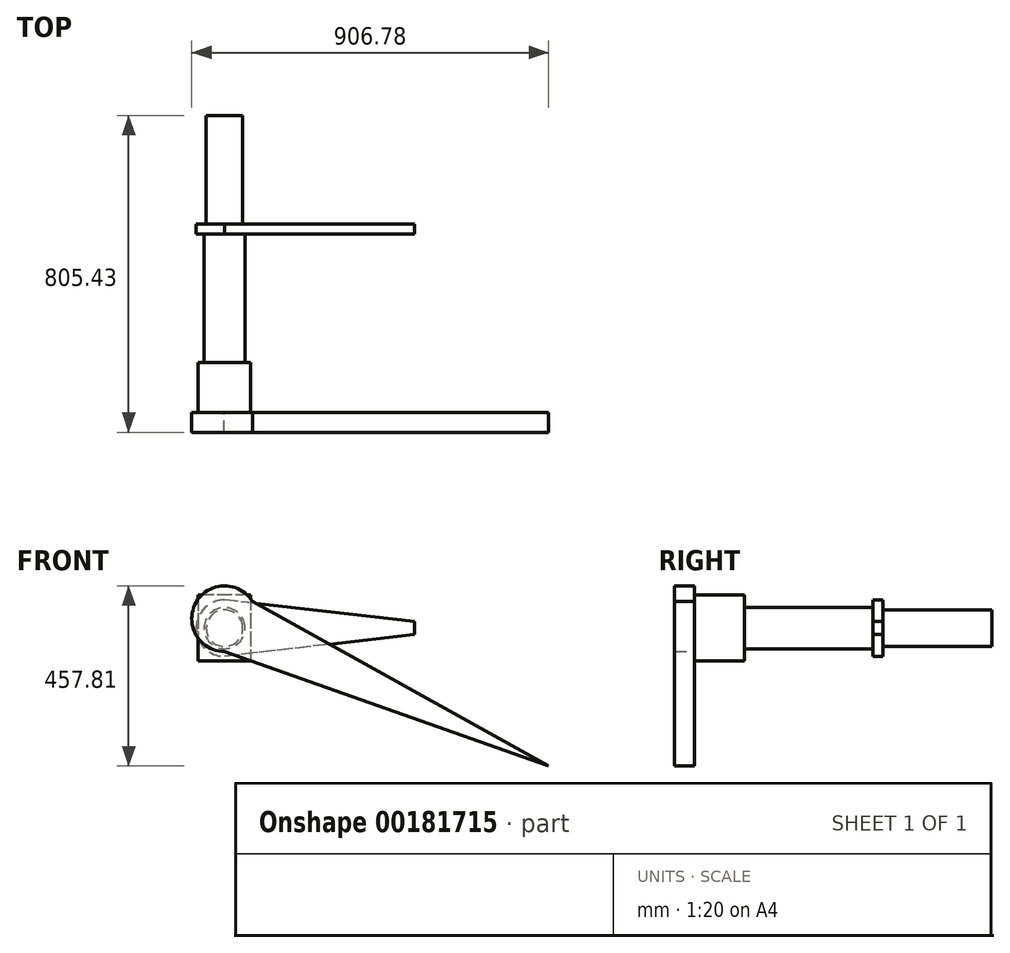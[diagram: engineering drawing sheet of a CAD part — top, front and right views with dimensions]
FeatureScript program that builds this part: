
annotation { "Feature Type Name" : "Feature", "Feature Type Description" : "" }
export const myFeature = defineFeature(function(context is Context, id is Id, definition is map)
    precondition{}
    {
        {
            var Q0;
            Q0=qCreatedBy(makeId("Front.planeOp"),FACE);
            var sketch = newSketch(context, id + "F0", { "sketchPlane" : qUnion([Q0])});
            skCircle(sketch, "E0", {"center": v(0, 0) * mm, "radius": 46.39 * mm});
            skSolve(sketch);
        }
        {
            var Q0;
            Q0 = qSketchRegion(id + "F0", true);
            extrude(context, id + "F7", {"entities" : qUnion([Q0]), "depth" : 276.6 * mm});
        }
        {
            var Q0;
            Q0=makeQuery(id+"F7.opExtrude","CAP_FACE",FACE,{"disambiguationData":[OSD([sQuery(id+"F0.wireOp",EDGE,"E0")])],"isStart":false});
            var sketch = newSketch(context, id + "F8", { "sketchPlane" : qUnion([Q0])});
            skCircle(sketch, "E1", {"center": v(0, 0) * mm, "radius": 71.79 * mm});
            skLineSegment(sketch, "E2", {"start": v(0, 0) * mm, "end": v(482.96, 0) * mm, "construction": true});
            skLineSegment(sketch, "E3", {"start": v(482.96, 16.57) * mm, "end": v(482.96, -15.59) * mm});
            skLineSegment(sketch, "E4", {"start": v(482.96, 16.57) * mm, "end": v(0, 71.79) * mm});
            skLineSegment(sketch, "E5", {"start": v(482.96, -15.59) * mm, "end": v(0, -71.79) * mm});
            skPoint(sketch, "E6.orphan", {"position": v(482.96, -71.79) * mm});
            skPoint(sketch, "E7.orphan", {"position": v(482.96, 71.79) * mm});
            skSolve(sketch);
        }
        {
            var Q0;
            {var subQ5=sQuery(id+"F8.wireOp",EDGE,"E3");Q0=makeQuery(id+"F8.imprint","IMPRINT",FACE,{"disambiguationData":[TD([[makeQuery(id+"F8.imprint","IMPRINT",EDGE,{"derivedFrom":subQ5}),-1.0]])]});}
            var Q1;
            Q1=makeQuery(id+"F8.imprint","IMPRINT",FACE,{"disambiguationData":[TD([[makeQuery(id+"F8.imprint","IMPRINT",EDGE,{"derivedFrom":makeQuery(id+"F7.opExtrude","CAP_EDGE",EDGE,{"disambiguationData":[OSD([sQuery(id+"F0.wireOp",EDGE,"E0")])],"isStart":false})}),1.0]])]});
            var Q2;
            Q2=makeQuery(id+"F8.imprint","IMPRINT",FACE,{"disambiguationData":[TD([[makeQuery(id+"F8.imprint","IMPRINT",EDGE,{"derivedFrom":makeQuery(id+"F7.opExtrude","CAP_EDGE",EDGE,{"disambiguationData":[OSD([sQuery(id+"F0.wireOp",EDGE,"E0")])],"isStart":false})}),-1.0]])]});
            extrude(context, id + "F1", {"entities" : qUnion([Q0, Q1, Q2]), "operationType" : NewBodyOperationType.ADD, "depth" : 25.4 * mm});
        }
        {
            var Q0;
            Q0=makeQuery(id+"F1.opExtrude","CAP_FACE",FACE,{"disambiguationData":[OSD([sQuery(id+"F8.wireOp",EDGE,"E1"),sQuery(id+"F8.wireOp",EDGE,"E3"),sQuery(id+"F8.wireOp",EDGE,"E4"),sQuery(id+"F8.wireOp",EDGE,"E5")])],"isStart":false});
            var sketch = newSketch(context, id + "F2", { "sketchPlane" : qUnion([Q0])});
            skCircle(sketch, "E8", {"center": v(0, 0) * mm, "radius": 52.12 * mm});
            skSolve(sketch);
        }
        {
            var Q0;
            Q0 = qSketchRegion(id + "F2", true);
            extrude(context, id + "F3", {"entities" : qUnion([Q0]), "operationType" : NewBodyOperationType.ADD, "depth" : 325.63 * mm});
        }
        {
            var Q0;
            Q0=makeQuery(id+"F3.opExtrude","CAP_FACE",FACE,{"disambiguationData":[OSD([sQuery(id+"F2.wireOp",EDGE,"E8")])],"isStart":false});
            var sketch = newSketch(context, id + "F4", { "sketchPlane" : qUnion([Q0])});
            skLineSegment(sketch, "E9.bottom", {"start": v(65.59, 84.23) * mm, "end": v(-66.78, 84.23) * mm});
            skLineSegment(sketch, "E9.top", {"start": v(65.59, -83.07) * mm, "end": v(-66.78, -83.07) * mm});
            skLineSegment(sketch, "E9.left", {"start": v(65.59, 84.23) * mm, "end": v(65.59, -83.07) * mm});
            skLineSegment(sketch, "E9.right", {"start": v(-66.78, 84.23) * mm, "end": v(-66.78, -83.07) * mm});
            skSolve(sketch);
        }
        {
            var Q0;
            Q0 = qSketchRegion(id + "F4", true);
            extrude(context, id + "F5", {"entities" : qUnion([Q0]), "operationType" : NewBodyOperationType.ADD, "depth" : 127 * mm});
        }
        {
            var Q0;
            Q0=makeQuery(id+"F5.opExtrude","CAP_FACE",FACE,{"disambiguationData":[OSD([sQuery(id+"F4.wireOp",EDGE,"E9.bottom"),sQuery(id+"F4.wireOp",EDGE,"E9.top"),sQuery(id+"F4.wireOp",EDGE,"E9.left"),sQuery(id+"F4.wireOp",EDGE,"E9.right")])],"isStart":false});
            var sketch = newSketch(context, id + "F6", { "sketchPlane" : qUnion([Q0])});
            skCircle(sketch, "E10", {"center": v(0, 24.17) * mm, "radius": 83.2 * mm});
            skLineSegment(sketch, "E11", {"start": v(0, 24.17) * mm, "end": v(735.73, -253.14) * mm, "construction": true});
            skLineSegment(sketch, "E12", {"start": v(55.98, 85.72) * mm, "end": v(-0.6, 107.37) * mm});
            skPoint(sketch, "E12.endSnap0", {"position": v(-0.6, 84.23) * mm});
            skLineSegment(sketch, "E13", {"start": v(-0.6, 107.37) * mm, "end": v(823.58, -350.44) * mm});
            skLineSegment(sketch, "E14", {"start": v(823.58, -350.44) * mm, "end": v(-0.6, -59.03) * mm});
            skPoint(sketch, "E14.endSnap0", {"position": v(-0.6, -83.07) * mm});
            skLineSegment(sketch, "E15", {"start": v(823.58, -350.44) * mm, "end": v(823.58, -350.44) * mm});
            skPoint(sketch, "E16.orphan", {"position": v(735.73, -174.35) * mm});
            skSolve(sketch);
        }
        {
            var Q0;
            Q0 = qSketchRegion(id + "F6", true);
            extrude(context, id + "F9", {"entities" : qUnion([Q0]), "operationType" : NewBodyOperationType.ADD, "depth" : 50.8 * mm});
        }
    });
